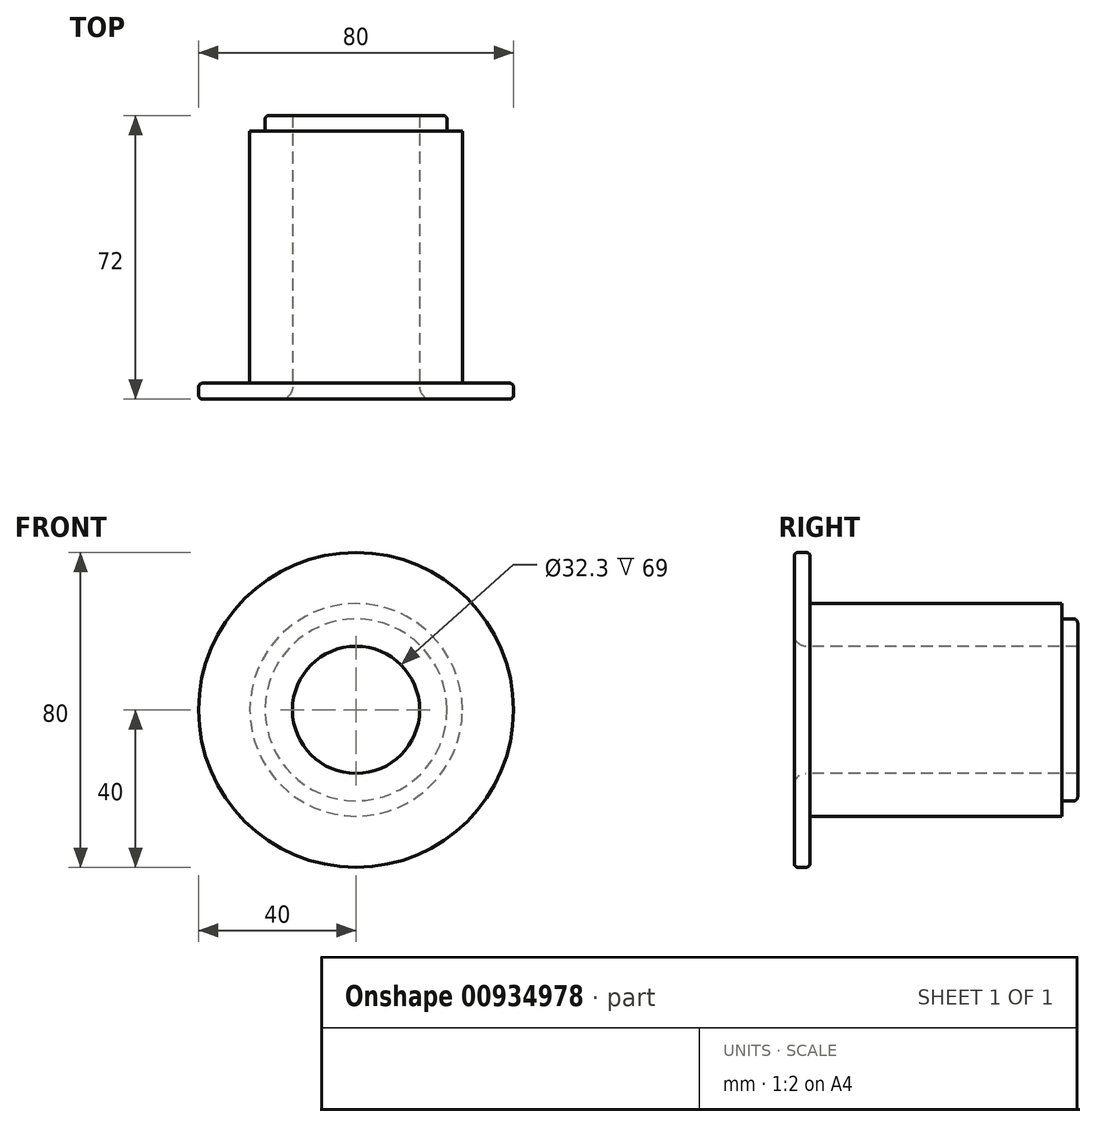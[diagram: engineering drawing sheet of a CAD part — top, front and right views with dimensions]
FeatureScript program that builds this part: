
annotation { "Feature Type Name" : "Feature", "Feature Type Description" : "" }
export const myFeature = defineFeature(function(context is Context, id is Id, definition is map)
    precondition{}
    {
        {
            var Q0;
            Q0=qCreatedBy(makeId("Right.planeOp"),FACE);
            var sketch = newSketch(context, id + "F0", { "sketchPlane" : qUnion([Q0])});
            skLineSegment(sketch, "E0", {"start": v(0, 0) * mm, "end": v(72, 0) * mm, "construction": true});
            skLineSegment(sketch, "E1", {"start": v(0, 0) * mm, "end": v(0, 39) * mm});
            skLineSegment(sketch, "E2", {"start": v(1, 40) * mm, "end": v(3, 40) * mm});
            skLineSegment(sketch, "E3", {"start": v(4, 39) * mm, "end": v(4, 27) * mm});
            skLineSegment(sketch, "E4", {"start": v(4, 0) * mm, "end": v(0, 0) * mm});
            skLineSegment(sketch, "E5.bottom", {"start": v(72, 0) * mm, "end": v(68, 0) * mm});
            skLineSegment(sketch, "E5.left", {"start": v(72, 16.15) * mm, "end": v(72, 23.11) * mm});
            skLineSegment(sketch, "E6", {"start": v(4, 27) * mm, "end": v(68, 27) * mm});
            skLineSegment(sketch, "E7", {"start": v(4, 16.15) * mm, "end": v(72, 16.15) * mm});
            skPoint(sketch, "E8.visualSharp", {"position": v(0, 40) * mm});
            skArc(sketch, "E8.filletArc", {"start": v(1, 40) * mm, "mid": v(0.3, 39.7) * mm, "end": v(0, 39) * mm});
            skPoint(sketch, "E9.visualSharp", {"position": v(4, 40) * mm});
            skArc(sketch, "E9.filletArc", {"start": v(4, 39) * mm, "mid": v(3.7, 39.7) * mm, "end": v(3, 40) * mm});
            skPoint(sketch, "E10.orphan", {"position": v(0, 16.15) * mm});
            skLineSegment(sketch, "E11.trimOffspring", {"start": v(4, 16.15) * mm, "end": v(4, 0) * mm});
            skLineSegment(sketch, "E12.0", {"start": v(68, 16.15) * mm, "end": v(68, 16.15) * mm});
            skLineSegment(sketch, "E13", {"start": v(68, 16.15) * mm, "end": v(68, 27) * mm, "construction": true});
            skLineSegment(sketch, "E14.0", {"start": v(68, 23.11) * mm, "end": v(72, 23.11) * mm});
            skLineSegment(sketch, "E15", {"start": v(68, 27) * mm, "end": v(68, 23.11) * mm});
            skSolve(sketch);
        }
        {
            var Q0;
            Q0=makeQuery(id+"F0.imprint","IMPRINT",FACE,{"disambiguationData":[TD([[makeQuery(id+"F0.imprint","IMPRINT",EDGE,{"derivedFrom":sQuery(id+"F0.wireOp",EDGE,"E1")}),-1.0]])]});
            var Q1;
            Q1=sQuery(id+"F0.wireOp",EDGE,"E0");
            revolve(context, id + "F1", {"surfaceOperationType" : NewSurfaceOperationType.NEW, "entities" : qUnion([Q0]), "axis" : qUnion([Q1]), "revolveType" : RevolveType.FULL});
        }
        {
            var Q0;
            Q0=makeQuery(id+"F1.opRevolve","SWEPT_FACE",FACE,{"disambiguationData":[OSD([sQuery(id+"F0.wireOp",EDGE,"E11.trimOffspring")])]});
            extrude(context, id + "F2", {"entities" : qUnion([Q0]), "operationType" : NewBodyOperationType.REMOVE, "endBound" : BoundingType.THROUGH_ALL, "oppositeDirection" : true, "depth" : 25 * mm, "offsetDistance" : 25 * mm});
        }
        {
            var Q0;
            Q0=makeQuery(id+"F2.boolean.opBoolean","INTERSECT",EDGE,{"derivedFrom":[makeQuery(id+"F1.opRevolve","SWEPT_FACE",FACE,{"disambiguationData":[OSD([sQuery(id+"F0.wireOp",EDGE,"E1")])]}),makeQuery(id+"F2.opExtrude","SWEPT_FACE",FACE,{"disambiguationData":[OSD([sQuery(id+"F0.wireOp",EDGE,"E7"),sQuery(id+"F0.wireOp",EDGE,"E11.trimOffspring")])]})]});
            fillet(context, id + "F3", {"entities" : qUnion([Q0]), "radius" : 3 * mm, "tangentPropagation" : true, "allowEdgeOverflow" : false});
        }
        {
            var Q0;
            Q0=makeQuery(id+"F1.opRevolve","SWEPT_EDGE",EDGE,{"disambiguationData":[OSD([sQuery(id+"F0.wireOp",EDGE,"E5.left"),sQuery(id+"F0.wireOp",EDGE,"E14.0")])]});
            fillet(context, id + "F4", {"entities" : qUnion([Q0]), "radius" : 1 * mm, "tangentPropagation" : true, "allowEdgeOverflow" : false});
        }
    });
